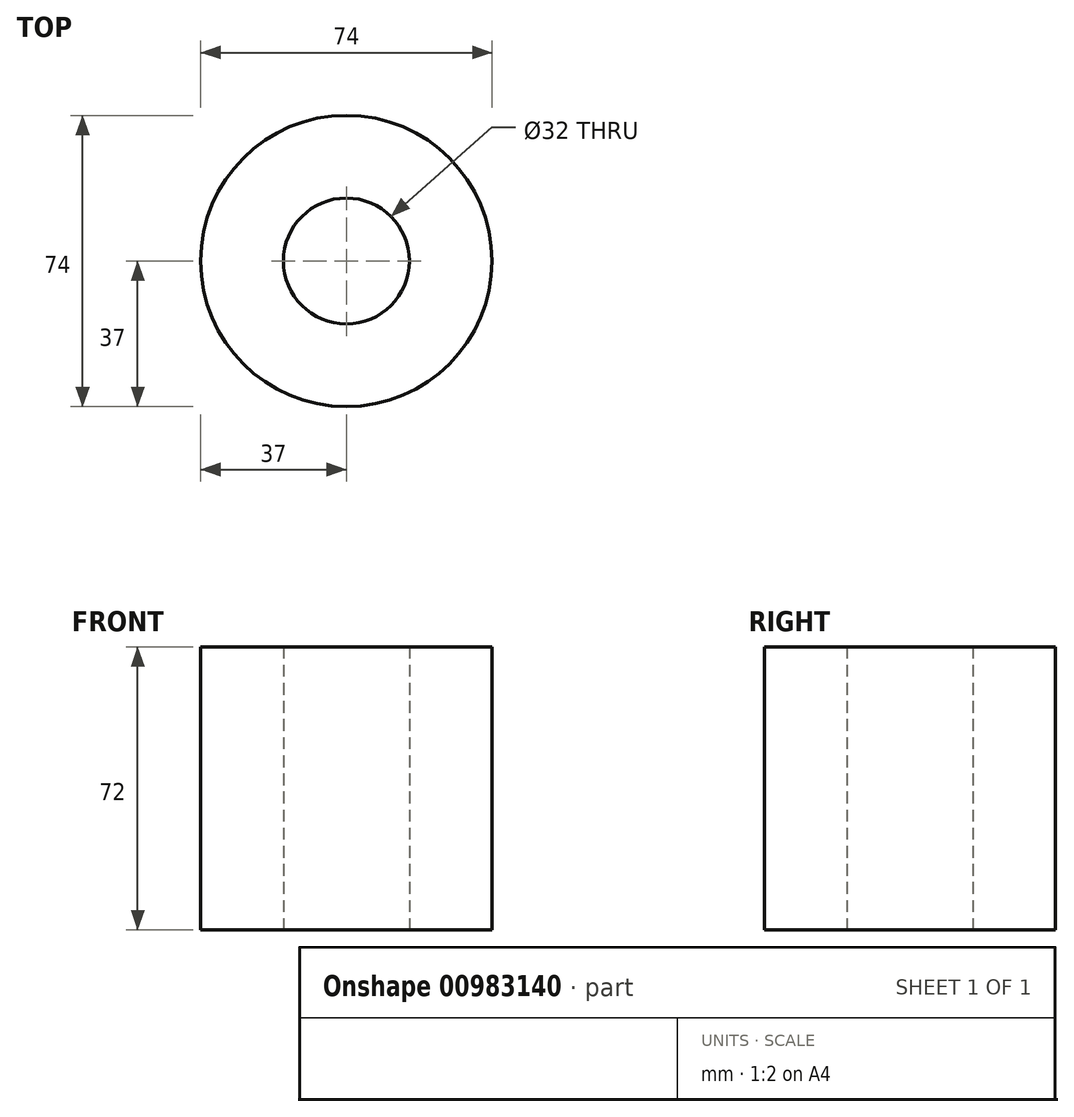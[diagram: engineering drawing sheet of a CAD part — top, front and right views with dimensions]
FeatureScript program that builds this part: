
annotation { "Feature Type Name" : "Feature", "Feature Type Description" : "" }
export const myFeature = defineFeature(function(context is Context, id is Id, definition is map)
    precondition{}
    {
        {
            var Q0;
            Q0=qCreatedBy(makeId("Top.planeOp"),FACE);
            var sketch = newSketch(context, id + "F0", { "sketchPlane" : qUnion([Q0])});
            skCircle(sketch, "E0", {"center": v(0, 0) * mm, "radius": 16 * mm});
            skCircle(sketch, "E1", {"center": v(0, 0) * mm, "radius": 37 * mm});
            skSolve(sketch);
        }
        {
            var Q0;
            Q0=makeQuery(id+"F0.imprint","IMPRINT",FACE,{"disambiguationData":[TD([[makeQuery(id+"F0.imprint","IMPRINT",EDGE,{"derivedFrom":sQuery(id+"F0.wireOp",EDGE,"E0")}),-1.0]])]});
            extrude(context, id + "F1", {"entities" : qUnion([Q0]), "depth" : 72 * mm, "offsetDistance" : 25 * mm});
        }
    });
